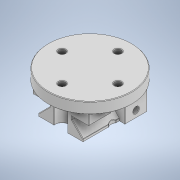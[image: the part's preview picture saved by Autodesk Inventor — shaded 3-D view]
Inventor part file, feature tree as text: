
AUTODESK INVENTOR PART (.ipt)
format: ipt  version: 2021 (Build 250183000, 183)  size: 509,952 bytes
history: native  units: mm
features: extrude x7, sketch x5, fillet x2, plane x1, mirror x1
ambient origin geometry x8: Origin, YZ Plane, XZ Plane, XY Plane, X Axis, Y Axis, Z Axis, Center Point
bodies: Solid1 (feature_tree)
feature tree (16):
  extrude  "Extrusion1"  Depth=52.5mm
  extrude  "Extrusion2"  Depth=26.25mm
  plane  "Work Plane1"
  mirror  "Mirror1"
  extrude  "Extrusion3"  Depth=5.0mm
  extrude  "Extrusion4"  TaperAngle=90.0deg  [1 undecoded]
  sketch  "Sketch6"  dims[d9=10.0mm d10=10.0mm d11=2.5mm d12=32.5mm d13=0.0mm d14=5.0mm d15=6.25mm d16=10.0mm d17=0.0mm d18=0.0mm d19=75.0mm d20=10.0mm d21=0.0mm d22=12.0mm d23=6.0mm d24=25.0mm d25=40.0mm d27=360.0deg d29=5.0mm d30=0.0mm d31=0.0mm d32=0.0mm d33=0.0mm d34=0.0mm d35=0.5mm d36=0.5mm]
  extrude  "Extrusion5"  Depth=10.0mm
  extrude  "Extrusion6"  Depth=0.5mm
  extrude  "Extrusion7"  Depth=0.5mm TaperAngle=0.0deg
  fillet  "Fillet1"  Radius=5.0mm
  fillet  "Fillet2"  Radius=6.25mm
  sketch  "Sketch1"  dims[d0=50.0mm d1=52.5mm]
  sketch  "Sketch2"  dims[d2=25.0mm d3=26.25mm]
  sketch  "Sketch3"  dims[d4=25.0mm d5=0.0mm d6=5.0mm]
  sketch  "Sketch4"  dims[d7=2.5mm d8=90.0deg]
note: 1 required parameter value undecoded (feature->parameter linkage not recoverable at this tier; creation-order binding heuristic only, values carry confidence <= 0.55)
